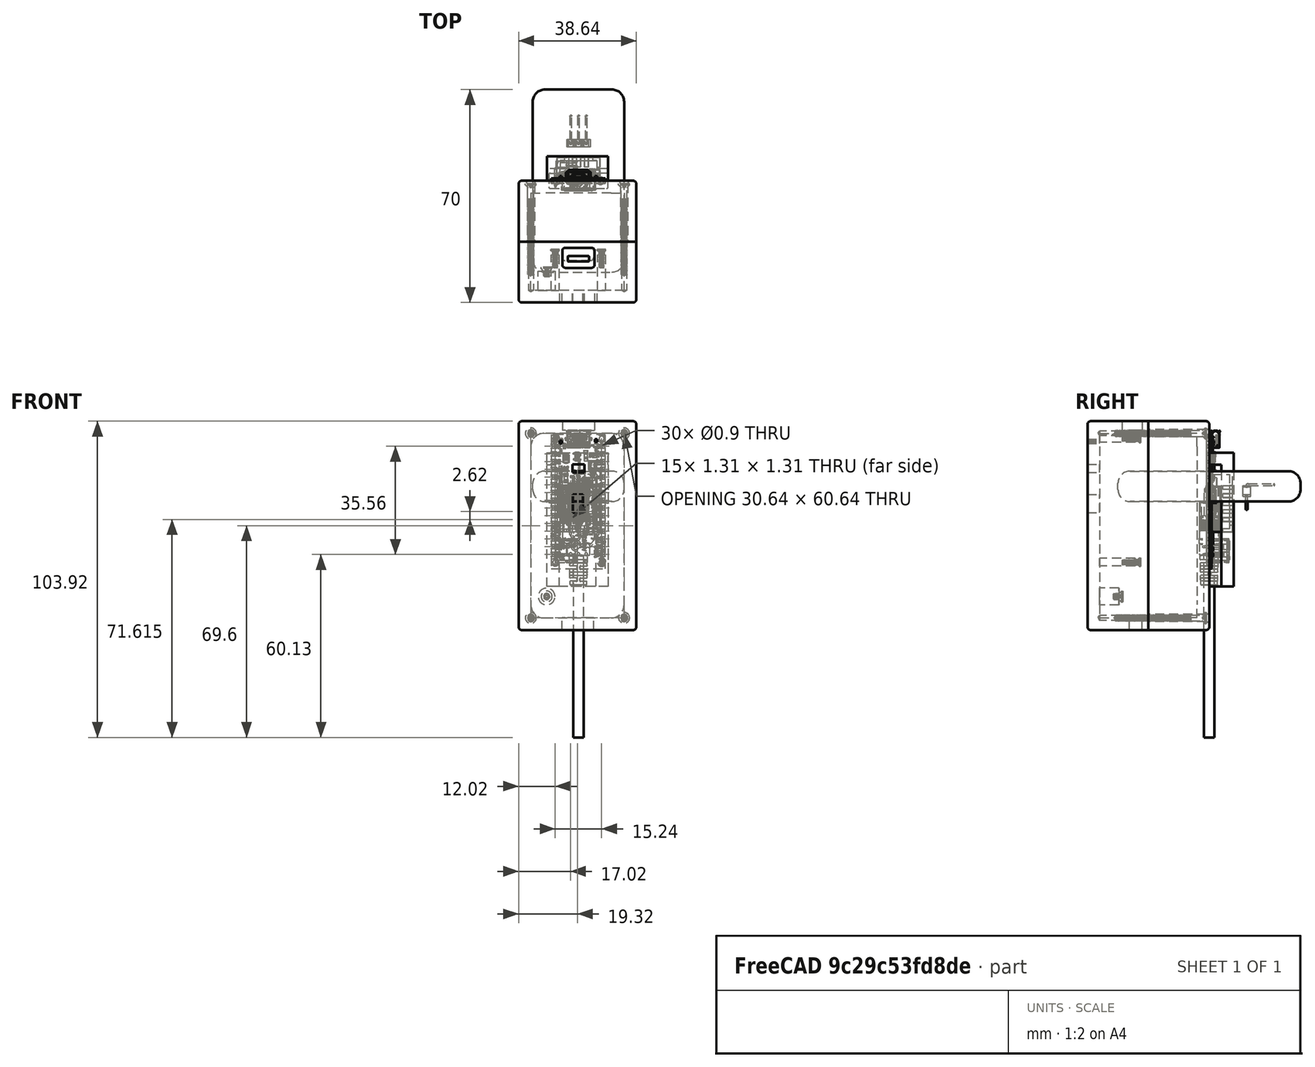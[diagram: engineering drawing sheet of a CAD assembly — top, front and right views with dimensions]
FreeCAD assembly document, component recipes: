
FREECAD ASSEMBLY — COMPONENT RECIPES ("iot_assembly")

This assembly document has 7 components, labeled P0..P6 below (a component is one placed body or linked part). 3 of them carry a construction recipe — the FreeCAD feature program that regenerates the part from scratch, quoted from this document or its linked companion documents; the rest are supplied as boundary geometry only. No exploded tour is included for this assembly.
COMPONENT P0 — geometry summary ("Part_ArduinoNano33IoT"; no construction recipe available for this part):
  bounding box: 45.3 x 17.8 x 5.6 mm
  tessellated surface: 86,666 triangles
  volume: 1530 mm^3 (34% of its bounding box)
COMPONENT P1 — geometry summary ("Part_DHT22Modulev3"; no construction recipe available for this part):
  bounding box: 25.6 x 14.0 x 7.7 mm
  tessellated surface: 5,666 triangles
  volume: 894 mm^3 (32% of its bounding box)
  symmetry: mirror-symmetric across its z mid-plane
COMPONENT P2 — geometry summary ("Part_MicroUSBCable"; no construction recipe available for this part):
  bounding box: 83.5 x 10.6 x 6.6 mm
  tessellated surface: 36,642 triangles
  volume: 1833 mm^3 (31% of its bounding box)
  symmetry: 2-fold rotationally symmetric about the z axis; mirror-symmetric across its x mid-plane, y mid-plane
COMPONENT P3 — recipe-attached ("Part_Battery", modeled in this document).
Construction recipe (the document's own serialized feature program — sketch geometry with constraints, then the solid features built on it; lengths are millimeters unless a unit is written):

FEATURE [Sketcher::SketchObject] Sketch
  ArcFitTolerance = 1e-06
  AttachmentSupport = -> [XY_Plane008]
  FullyConstrained = true
  MakeInternals = false
  MapMode = 5
  expr: Constraints[8] = <<Spreadsheet_Battery>>.BatteryWidth
  expr: Constraints[9] = <<Spreadsheet_Battery>>.BatteryLength
  sketch-geometry (4):
    g0: LineSegment StartX=-15 StartY=30 StartZ=0 EndX=-15 EndY=-30 EndZ=0
    g1: LineSegment StartX=-15 StartY=-30 StartZ=0 EndX=15 EndY=-30 EndZ=0
    g2: LineSegment StartX=15 StartY=-30 StartZ=0 EndX=15 EndY=30 EndZ=0
    g3: LineSegment StartX=15 StartY=30 StartZ=0 EndX=-15 EndY=30 EndZ=0
  constraints (11):
    c: Coincident(g0,g1)
    c: Coincident(g1,g2)
    c: Coincident(g2,g3)
    c: Coincident(g3,g0)
    c: Vertical(g0)
    c: Vertical(g2)
    c: Horizontal(g1)
    c: Horizontal(g3)
    c: DistanceX(g3,g3) = 30
    c: DistanceY(g0,g0) = 60
    c: Symmetric(g0,g1,g-1)
FEATURE [PartDesign::Pad] Pad
  Direction = (0,0,1)
  Length = 10
  Length2 = 10
  Profile = -> Sketch
  ReferenceAxis = -> Sketch [N_Axis]
  Refine = true
  Suppressed = false
  Type = 0
  expr: Length = <<Spreadsheet_Battery>>.BatteryHeight
FEATURE [PartDesign::Fillet] Fillet
  Base = -> Pad [Face6,Face5,Face4,Face1]
  BaseFeature = -> Pad
  Radius = 4
  Refine = true
  SupportTransform = false
  Suppressed = false
  UseAllEdges = true
FEATURE [PartDesign::Body] Body  label="Body_Battery"
  AllowCompound = false
  Group = -> [Sketch,Pad,Fillet]
  Origin = -> Origin008
  Tip = -> Fillet
COMPONENT P4 — recipe-attached ("Part_EnclosureBottom", modeled in this document).
Construction recipe (the document's own serialized feature program — sketch geometry with constraints, then the solid features built on it; lengths are millimeters unless a unit is written):

FEATURE [PartDesign::SubShapeBinder] Binder  label="Binder_Battery"
  BindCopyOnChange = 0
  BindMode = 0
  ClaimChildren = false
  Context = -> Assembly001 [Assembly002.Part001.Body001.Binder.]
  Fuse = false
  MakeFace = true
  OffsetFill = false
  OffsetIntersection = false
  OffsetJoinType = 0
  OffsetOpenResult = false
  PartialLoad = false
  Refine = true
  Relative = true
  Support = -> [Part]
  _Version = 2
FEATURE [Sketcher::SketchObject] Sketch001
  ArcFitTolerance = 1e-06
  AttachmentSupport = -> [XZ_Plane010]
  ExternalGeometry = -> [Binder]
  FullyConstrained = true
  MakeInternals = false
  MapMode = 5
  Placement = pos=(0,0,0) rot=(1,0,0;1.5708rad)
  expr: Constraints[10] = <<Spreadsheet_Enclosure>>.EnclosureWallThickness + <<Spreadsheet_Enclosure>>.EnclosureWallThicknessTolerance
  expr: Constraints[11] = <<Spreadsheet_Enclosure>>.EnclosureWallThickness + <<Spreadsheet_Enclosure>>.EnclosureWallThicknessTolerance
  expr: Constraints[8] = <<Spreadsheet_Enclosure>>.EnclosureWallThickness + <<Spreadsheet_Enclosure>>.EnclosureWallThicknessTolerance
  expr: Constraints[9] = <<Spreadsheet_Enclosure>>.EnclosureWallThickness + <<Spreadsheet_Enclosure>>.EnclosureWallThicknessTolerance
  sketch-geometry (4):
    g0: LineSegment StartX=-19.64 StartY=26.42 StartZ=0 EndX=-19.64 EndY=-42.22 EndZ=0
    g1: LineSegment StartX=-19.64 StartY=-42.22 StartZ=0 EndX=19 EndY=-42.22 EndZ=0
    g2: LineSegment StartX=19 StartY=-42.22 StartZ=0 EndX=19 EndY=26.42 EndZ=0
    g3: LineSegment StartX=19 StartY=26.42 StartZ=0 EndX=-19.64 EndY=26.42 EndZ=0
  constraints (12):
    c: Coincident(g0,g1)
    c: Coincident(g1,g2)
    c: Coincident(g2,g3)
    c: Coincident(g3,g0)
    c: Vertical(g0)
    c: Vertical(g2)
    c: Horizontal(g1)
    c: Horizontal(g3)
    c: Distance(g3,g-4) = 4.32
    c: Distance(g-10,g0) = 4.32
    c: Distance(g-6,g2) = 4.32
    c: Distance(g-8,g1) = 4.32
FEATURE [PartDesign::Pad] Pad001  label="EnclosureBottom"
  Direction = (0,-1,2e-16)
  Length = 20
  Length2 = 10
  Placement = pos=(0,0,0) rot=(1,0,0;1.5708rad)
  Profile = -> Sketch001
  ReferenceAxis = -> Sketch001 [N_Axis]
  Refine = true
  Suppressed = false
  Type = 0
  expr: Length = <<Spreadsheet_Enclosure>>.EnclosureBottomDepth
FEATURE [PartDesign::Thickness] Thickness  label="EnclosureWallThickness001"
  Base = -> Pad001 [Face6]
  BaseFeature = -> Pad001
  Intersection = false
  Join = 0
  Mode = 0
  Refine = true
  Reversed = true
  SupportTransform = false
  Suppressed = false
  Value = 4
  expr: Value = <<Spreadsheet_Enclosure>>.EnclosureWallThickness
FEATURE [PartDesign::Fillet] Fillet002  label="EnclosureFillet001"
  Base = -> Thickness [Edge1,Edge8,Edge5,Edge2,Edge3,Edge6,Edge9,Edge11]
  BaseFeature = -> Thickness
  Radius = 1
  Refine = true
  SupportTransform = false
  Suppressed = false
  UseAllEdges = false
  expr: Radius = <<Spreadsheet_Enclosure>>.EnclosureBevel
FEATURE [Sketcher::SketchObject] Sketch012
  ArcFitTolerance = 1e-06
  AttachmentSupport = -> [Fillet002]
  ExternalGeometry = -> [Binder,Fillet002]
  FullyConstrained = true
  MakeInternals = false
  MapMode = 5
  Placement = pos=(0,-4,0) rot=(1,0,0;1.5708rad)
  expr: Constraints[14] = <<Spreadsheet_Enclosure>>.EnclosureWallThickness + <<Spreadsheet_Enclosure>>.EnclosureWallThicknessTolerance
  expr: Constraints[1] = <<Spreadsheet_Enclosure>>.EnclosureWallThickness + <<Spreadsheet_Enclosure>>.EnclosureWallThicknessTolerance
  expr: Constraints[20] = <<Spreadsheet_Enclosure>>.EnclosureWallThickness + <<Spreadsheet_Enclosure>>.EnclosureWallThicknessTolerance
  expr: Constraints[8] = <<Spreadsheet_Enclosure>>.EnclosureWallThickness + <<Spreadsheet_Enclosure>>.EnclosureWallThicknessTolerance
  sketch-geometry (12):
    g0: ArcOfCircle CenterX=-11.32 CenterY=18.1 CenterZ=0 NormalX=0 NormalY=0 NormalZ=1 AngleXU=0 Radius=4.32 StartAngle=1.5708 EndAngle=3.14159
    g1: LineSegment StartX=-15.64 StartY=22.42 StartZ=0 EndX=-15.64 EndY=18.1 EndZ=0
    g2: LineSegment StartX=-11.32 StartY=22.42 StartZ=0 EndX=-15.64 EndY=22.42 EndZ=0
    g3: ArcOfCircle CenterX=10.68 CenterY=18.1 CenterZ=0 NormalX=0 NormalY=0 NormalZ=1 AngleXU=0 Radius=4.32 StartAngle=8.06468e-08 EndAngle=1.5708
    g4: LineSegment StartX=15 StartY=22.42 StartZ=0 EndX=15 EndY=18.1 EndZ=0
    g5: LineSegment StartX=10.68 StartY=22.42 StartZ=0 EndX=15 EndY=22.42 EndZ=0
    g6: ArcOfCircle CenterX=10.68 CenterY=-33.9 CenterZ=0 NormalX=0 NormalY=0 NormalZ=1 AngleXU=0 Radius=4.32 StartAngle=4.71239 EndAngle=6.28319
    g7: LineSegment StartX=10.68 StartY=-38.22 StartZ=0 EndX=15 EndY=-38.22 EndZ=0
    g8: LineSegment StartX=15 StartY=-38.22 StartZ=0 EndX=15 EndY=-33.9 EndZ=0
    g9: LineSegment StartX=-15.64 StartY=-38.22 StartZ=0 EndX=-15.64 EndY=-33.9 EndZ=0
    g10: ArcOfCircle CenterX=-11.32 CenterY=-33.9 CenterZ=0 NormalX=0 NormalY=0 NormalZ=1 AngleXU=0 Radius=4.32 StartAngle=3.14159 EndAngle=4.71239
    g11: LineSegment StartX=-11.32 StartY=-38.22 StartZ=0 EndX=-15.64 EndY=-38.22 EndZ=0
  constraints (32):
    c: Coincident(g0,g-3)
    c: Radius(g0) = 4.32
    c: Coincident(g2,g1)
    c: Vertical(g1)
    c: Horizontal(g2)
    c: Coincident(g1,g-5)
    c: Coincident(g0,g2)
    c: Coincident(g0,g1)
    c: Radius(g3) = 4.32
    c: Coincident(g5,g4)
    c: Vertical(g4)
    c: Horizontal(g5)
    c: Coincident(g3,g5)
    c: Coincident(g3,g4)
    c: Radius(g10) = 4.32
    c: Coincident(g11,g9)
    c: Vertical(g9)
    c: Horizontal(g11)
    c: Coincident(g10,g11)
    c: Coincident(g10,g9)
    c: Radius(g6) = 4.32
    c: Coincident(g7,g8)
    c: Vertical(g8)
    c: Horizontal(g7)
    c: Coincident(g6,g7)
    c: Coincident(g6,g8)
    c: Coincident(g-6,g3)
    c: Coincident(g4,g-9)
    c: Coincident(g7,g-10)
    c: Coincident(g6,g-8)
    c: Coincident(g9,g-10)
    c: Coincident(g10,g-7)
FEATURE [PartDesign::Pad] Pad006  label="EnclosureReinforcement"
  BaseFeature = -> Fillet002
  Direction = (0,-1,2e-16)
  Length = 10
  Length2 = 10
  Profile = -> Sketch012
  ReferenceAxis = -> Sketch012 [N_Axis]
  Refine = true
  Suppressed = false
  Type = 3
  UpToFace = -> Fillet002 [Face2]
FEATURE [Sketcher::SketchObject] Sketch013
  ArcFitTolerance = 1e-06
  AttachmentSupport = -> [Pad006]
  ExternalGeometry = -> [Pad006]
  FullyConstrained = true
  MakeInternals = false
  MapMode = 5
  Placement = pos=(0,-1.8e-15,0) rot=(0,0.707107,0.707107;3.14159rad)
  expr: Constraints[0] = <<Spreadsheet_Enclosure>>.EnclosureScrewHoles
  expr: Constraints[3] = <<Spreadsheet_Enclosure>>.EnclosureScrewHoles
  expr: Constraints[6] = <<Spreadsheet_Enclosure>>.EnclosureScrewHoles
  expr: Constraints[7] = <<Spreadsheet_Enclosure>>.EnclosureScrewHoles
  sketch-geometry (4):
    g0: Circle CenterX=-15 CenterY=22.42 CenterZ=0 NormalX=0 NormalY=0 NormalZ=1 AngleXU=0 Radius=1
    g1: Circle CenterX=15.64 CenterY=22.42 CenterZ=0 NormalX=0 NormalY=0 NormalZ=1 AngleXU=0 Radius=1
    g2: Circle CenterX=-15 CenterY=-38.22 CenterZ=0 NormalX=0 NormalY=0 NormalZ=1 AngleXU=0 Radius=1
    g3: Circle CenterX=15.64 CenterY=-38.22 CenterZ=0 NormalX=0 NormalY=0 NormalZ=1 AngleXU=0 Radius=1
  constraints (12):
    c: Diameter(g0) = 2
    c: Vertical(g0,g-8)
    c: Horizontal(g-9,g0)
    c: Diameter(g1) = 2
    c: Horizontal(g-10,g1)
    c: Vertical(g-11,g1)
    c: Diameter(g2) = 2
    c: Diameter(g3) = 2
    c: Vertical(g3,g-12)
    c: Horizontal(g3,g-13)
    c: Vertical(g-14,g2)
    c: Horizontal(g2,g-14)
FEATURE [PartDesign::Hole] Hole002  label="EnclosureScrewHoles"
  BaseFeature = -> Pad006
  CustomThreadClearance = 0
  Depth = 25
  DepthType = 0
  Diameter = 2.4
  DrillForDepth = false
  DrillPoint = 1
  DrillPointAngle = 118
  HoleCutCountersinkAngle = 90
  HoleCutCustomValues = false
  HoleCutDepth = 0
  HoleCutDiameter = 6.1
  HoleCutType = 0
  ModelThread = false
  Profile = -> Sketch013
  Refine = true
  Suppressed = false
  Tapered = false
  TaperedAngle = 90
  ThreadClass = 0
  ThreadDepth = 25
  ThreadDepthType = 0
  ThreadDirection = 0
  ThreadFit = 0
  ThreadSize = 6
  ThreadType = 1
  Threaded = false
  UseCustomThreadClearance = false
FEATURE [PartDesign::Fillet] Fillet004  label="EnclosureScrewHolesFillet"
  Base = -> Hole002 [Edge41,Edge45,Edge63,Edge43]
  BaseFeature = -> Hole002
  Radius = 1
  Refine = true
  SupportTransform = false
  Suppressed = false
  UseAllEdges = false
FEATURE [Sketcher::SketchObject] Sketch018
  ArcFitTolerance = 1e-06
  AttachmentSupport = -> [Fillet004]
  ExternalGeometry = -> [Fillet004]
  FullyConstrained = true
  MakeInternals = false
  MapMode = 5
  Placement = pos=(0,-1.8e-15,0) rot=(0,0.707107,0.707107;3.14159rad)
  expr: Constraints[8] = <<Spreadsheet_Enclosure>>.EnclosureSlidingMechanismWidth - <<Spreadsheet_Enclosure>>.EnclosureSlidingMechanismThickness * 2
  expr: Constraints[9] = <<Spreadsheet_Enclosure>>.EnclosureSlidingMechanismLength
  sketch-geometry (9):
    g0: LineSegment StartX=-5.68 StartY=12.1 StartZ=0 EndX=-5.68 EndY=-27.9 EndZ=0
    g1: LineSegment StartX=-5.68 StartY=-27.9 StartZ=0 EndX=6.32 EndY=-27.9 EndZ=0
    g2: LineSegment StartX=6.32 StartY=-27.9 StartZ=0 EndX=6.32 EndY=12.1 EndZ=0
    g3: LineSegment StartX=6.32 StartY=12.1 StartZ=0 EndX=-5.68 EndY=12.1 EndZ=0
    g4: LineSegment [constr] StartX=-18 StartY=25.42 StartZ=0 EndX=-18 EndY=-41.22 EndZ=0
    g5: LineSegment [constr] StartX=-18 StartY=-41.22 StartZ=0 EndX=18.64 EndY=-41.22 EndZ=0
    g6: LineSegment [constr] StartX=18.64 StartY=-41.22 StartZ=0 EndX=18.64 EndY=25.42 EndZ=0
    g7: LineSegment [constr] StartX=18.64 StartY=25.42 StartZ=0 EndX=-18 EndY=25.42 EndZ=0
    g8: GeomPoint [constr] X=0.32 Y=-7.9 Z=0
  constraints (22):
    c: Coincident(g0,g1)
    c: Coincident(g1,g2)
    c: Coincident(g2,g3)
    c: Coincident(g3,g0)
    c: Vertical(g0)
    c: Vertical(g2)
    c: Horizontal(g1)
    c: Horizontal(g3)
    c: DistanceX(g3,g3) = 12
    c: DistanceY(g0,g0) = 40
    c: Coincident(g4,g5)
    c: Coincident(g5,g6)
    c: Coincident(g6,g7)
    c: Coincident(g7,g4)
    c: Vertical(g4)
    c: Vertical(g6)
    c: Horizontal(g5)
    c: Horizontal(g7)
    c: Coincident(g4,g-3)
    c: Coincident(g5,g-4)
    c: Symmetric(g5,g4,g8)
    c: Symmetric(g0,g1,g8)
FEATURE [PartDesign::Pad] Pad008  label="EnclosureSlidingMechanismSupport"
  BaseFeature = -> Fillet004
  Direction = (0,1,-2e-16)
  Length = 4
  Length2 = 10
  Profile = -> Sketch018
  ReferenceAxis = -> Sketch018 [N_Axis]
  Refine = true
  Suppressed = false
  Type = 0
  expr: Length = <<Spreadsheet_Enclosure>>.EnclosureSlidingMechanismThickness
FEATURE [Sketcher::SketchObject] Sketch019
  ArcFitTolerance = 1e-06
  AttachmentSupport = -> [Pad008]
  ExternalGeometry = -> [Pad008]
  FullyConstrained = true
  MakeInternals = false
  MapMode = 5
  Placement = pos=(0,4,0) rot=(0,0.707107,0.707107;3.14159rad)
  expr: Constraints[8] = <<Spreadsheet_Enclosure>>.EnclosureSlidingMechanismWidth
  expr: Constraints[9] = <<Spreadsheet_Enclosure>>.EnclosureSlidingMechanismLength
  sketch-geometry (9):
    g0: LineSegment StartX=-9.68 StartY=12.1 StartZ=0 EndX=-9.68 EndY=-27.9 EndZ=0
    g1: LineSegment StartX=-9.68 StartY=-27.9 StartZ=0 EndX=10.32 EndY=-27.9 EndZ=0
    g2: LineSegment StartX=10.32 StartY=-27.9 StartZ=0 EndX=10.32 EndY=12.1 EndZ=0
    g3: LineSegment StartX=10.32 StartY=12.1 StartZ=0 EndX=-9.68 EndY=12.1 EndZ=0
    g4: LineSegment [constr] StartX=-18 StartY=25.42 StartZ=0 EndX=-18 EndY=-41.22 EndZ=0
    g5: LineSegment [constr] StartX=-18 StartY=-41.22 StartZ=0 EndX=18.64 EndY=-41.22 EndZ=0
    g6: LineSegment [constr] StartX=18.64 StartY=-41.22 StartZ=0 EndX=18.64 EndY=25.42 EndZ=0
    g7: LineSegment [constr] StartX=18.64 StartY=25.42 StartZ=0 EndX=-18 EndY=25.42 EndZ=0
    g8: GeomPoint [constr] X=0.32 Y=-7.9 Z=0
  constraints (22):
    c: Coincident(g0,g1)
    c: Coincident(g1,g2)
    c: Coincident(g2,g3)
    c: Coincident(g3,g0)
    c: Vertical(g0)
    c: Vertical(g2)
    c: Horizontal(g1)
    c: Horizontal(g3)
    c: DistanceX(g3,g3) = 20
    c: DistanceY(g0,g0) = 40
    c: Coincident(g4,g5)
    c: Coincident(g5,g6)
    c: Coincident(g6,g7)
    c: Coincident(g7,g4)
    c: Vertical(g4)
    c: Vertical(g6)
    c: Horizontal(g5)
    c: Horizontal(g7)
    c: Coincident(g4,g-3)
    c: Coincident(g5,g-4)
    c: Symmetric(g4,g5,g8)
    c: Symmetric(g1,g0,g8)
FEATURE [PartDesign::Pad] Pad009  label="EnclosureSlidingMechanismSupportMaleChannel"
  BaseFeature = -> Pad008
  Direction = (0,1,-2e-16)
  Length = 4
  Length2 = 10
  Profile = -> Sketch019
  ReferenceAxis = -> Sketch019 [N_Axis]
  Refine = true
  Suppressed = false
  Type = 0
  expr: Length = <<Spreadsheet_Enclosure>>.EnclosureSlidingMechanismChannel
FEATURE [Sketcher::SketchObject] Sketch020
  ArcFitTolerance = 1e-06
  AttachmentSupport = -> [Pad009]
  ExternalGeometry = -> [Pad009]
  FullyConstrained = true
  MakeInternals = false
  MapMode = 5
  Placement = pos=(0,0,12.1) rot=(0,0,1;0rad)
  sketch-geometry (4):
    g0: LineSegment StartX=-10.32 StartY=8 StartZ=0 EndX=-10.32 EndY=0 EndZ=0
    g1: LineSegment StartX=-10.32 StartY=0 StartZ=0 EndX=9.68 EndY=0 EndZ=0
    g2: LineSegment StartX=9.68 StartY=0 StartZ=0 EndX=9.68 EndY=8 EndZ=0
    g3: LineSegment StartX=9.68 StartY=8 StartZ=0 EndX=-10.32 EndY=8 EndZ=0
  constraints (11):
    c: Coincident(g0,g1)
    c: Coincident(g1,g2)
    c: Coincident(g2,g3)
    c: Coincident(g3,g0)
    c: Vertical(g0)
    c: Vertical(g2)
    c: Horizontal(g1)
    c: Horizontal(g3)
    c: Coincident(g0,g-3)
    c: Vertical(g1,g-4)
    c: Horizontal(g1,g-1)
FEATURE [PartDesign::Pad] Pad010  label="EnclosureSlidingMechanismStop"
  BaseFeature = -> Pad009
  Direction = (0,0,1)
  Length = 4
  Length2 = 10
  Profile = -> Sketch020
  ReferenceAxis = -> Sketch020 [N_Axis]
  Refine = true
  Suppressed = false
  Type = 0
  expr: Length = <<Spreadsheet_Enclosure>>.EnclosureSlidingMechanismThickness
FEATURE [PartDesign::Body] Body001  label="Body_EnclosureBottom"
  AllowCompound = false
  Group = -> [Binder,Sketch001,Pad001,Thickness,Fillet002,Sketch012,Pad006,Sketch013,Hole002,Fillet004,Sketch018,Pad008,Sketch019,Pad009,Sketch020,Pad010]
  Origin = -> Origin010
  Tip = -> Pad010
COMPONENT P5 — recipe-attached ("Part_EnclosureTop", modeled in this document).
Construction recipe (the document's own serialized feature program — sketch geometry with constraints, then the solid features built on it; lengths are millimeters unless a unit is written):

FEATURE [PartDesign::SubShapeBinder] Binder001  label="Binder_EnclosureBottom"
  BindCopyOnChange = 0
  BindMode = 0
  ClaimChildren = false
  Context = -> Assembly001 [Assembly002.Part002.Body002.Binder001.]
  Fuse = false
  MakeFace = true
  OffsetFill = false
  OffsetIntersection = false
  OffsetJoinType = 0
  OffsetOpenResult = false
  PartialLoad = false
  Refine = true
  Relative = true
  Support = -> [Part001]
  _Version = 2
FEATURE [Sketcher::SketchObject] Sketch002
  ArcFitTolerance = 1e-06
  AttachmentSupport = -> [Binder001]
  ExternalGeometry = -> [Binder001]
  FullyConstrained = true
  MakeInternals = false
  MapMode = 5
  Placement = pos=(0,-20,5.2e-15) rot=(1,0,0;1.5708rad)
  sketch-geometry (4):
    g0: LineSegment StartX=-19.64 StartY=26.42 StartZ=0 EndX=-19.64 EndY=-42.22 EndZ=0
    g1: LineSegment StartX=-19.64 StartY=-42.22 StartZ=0 EndX=19 EndY=-42.22 EndZ=0
    g2: LineSegment StartX=19 StartY=-42.22 StartZ=0 EndX=19 EndY=26.42 EndZ=0
    g3: LineSegment StartX=19 StartY=26.42 StartZ=0 EndX=-19.64 EndY=26.42 EndZ=0
  constraints (12):
    c: Coincident(g0,g1)
    c: Coincident(g1,g2)
    c: Coincident(g2,g3)
    c: Coincident(g3,g0)
    c: Vertical(g0)
    c: Vertical(g2)
    c: Horizontal(g1)
    c: Horizontal(g3)
    c: Horizontal(g0,g-4)
    c: Horizontal(g0,g-6)
    c: Vertical(g-5,g0)
    c: Vertical(g-7,g2)
FEATURE [PartDesign::Pad] Pad002  label="EnclosureTop"
  Direction = (0,-1,2e-16)
  Length = 20
  Length2 = 10
  Profile = -> Sketch002
  ReferenceAxis = -> Sketch002 [N_Axis]
  Refine = true
  Suppressed = false
  Type = 0
  expr: Length = <<Spreadsheet_Enclosure>>.EnclosureTopDepth
FEATURE [PartDesign::Thickness] Thickness001  label="EnclosureWallThickness"
  Base = -> Pad002 [Face5]
  BaseFeature = -> Pad002
  Intersection = false
  Join = 0
  Mode = 0
  Refine = true
  Reversed = true
  SupportTransform = false
  Suppressed = false
  Value = 4
  expr: Value = <<Spreadsheet_Enclosure>>.EnclosureWallThickness
FEATURE [PartDesign::SubShapeBinder] Binder002  label="Binder_ArduinoNano"
  BindCopyOnChange = 0
  BindMode = 0
  ClaimChildren = false
  Context = -> Assembly001 [Assembly002.Part002.Body002.Binder002.]
  Fuse = false
  MakeFace = true
  OffsetFill = false
  OffsetIntersection = false
  OffsetJoinType = 0
  OffsetOpenResult = false
  PartialLoad = false
  Refine = true
  Relative = true
  Support = -> [Assembly]
  _Version = 2
FEATURE [PartDesign::SubShapeBinder] Binder003  label="Binder_DHT22"
  BindCopyOnChange = 0
  BindMode = 0
  ClaimChildren = false
  Context = -> Assembly001 [Assembly002.Part002.Body002.Binder003.]
  Fuse = false
  MakeFace = true
  OffsetFill = false
  OffsetIntersection = false
  OffsetJoinType = 0
  OffsetOpenResult = false
  PartialLoad = false
  Refine = true
  Relative = true
  Support = -> [DHT22_Module_v3]
  _Version = 2
FEATURE [Sketcher::SketchObject] Sketch003
  ArcFitTolerance = 1e-06
  AttachmentSupport = -> [Thickness001,Binder002]
  ExternalGeometry = -> [Binder002]
  FullyConstrained = true
  MakeInternals = false
  MapMode = 5
  Placement = pos=(0,-36,9.4e-15) rot=(0,0.707107,0.707107;3.14159rad)
  sketch-geometry (4):
    g0: Circle CenterX=-7.62 CenterY=20.73 CenterZ=0 NormalX=0 NormalY=0 NormalZ=1 AngleXU=0 Radius=1.27
    g1: Circle CenterX=7.62 CenterY=20.73 CenterZ=0 NormalX=0 NormalY=0 NormalZ=1 AngleXU=0 Radius=1.27
    g2: Circle CenterX=-7.62 CenterY=-19.91 CenterZ=0 NormalX=0 NormalY=0 NormalZ=1 AngleXU=0 Radius=1.27
    g3: Circle CenterX=7.62 CenterY=-19.91 CenterZ=0 NormalX=0 NormalY=0 NormalZ=1 AngleXU=0 Radius=1.27
  constraints (8):
    c: Coincident(g0,g-3)
    c: Tangent(g0,g-7)
    c: Coincident(g1,g-13)
    c: Tangent(g1,g-5)
    c: Coincident(g2,g-12)
    c: Tangent(g2,g-11)
    c: Coincident(g3,g-8)
    c: Tangent(g3,g-9)
FEATURE [PartDesign::Pad] Pad003  label="PCBStandoffs"
  BaseFeature = -> Thickness001
  Direction = (0,1,-2e-16)
  Length = 10
  Length2 = 10
  Profile = -> Sketch003
  ReferenceAxis = -> Sketch003 [N_Axis]
  Refine = true
  Suppressed = false
  Type = 3
  UpToFace = -> Binder002 [Face2229]
FEATURE [Sketcher::SketchObject] Sketch004
  ArcFitTolerance = 1e-06
  AttachmentSupport = -> [Pad003]
  ExternalGeometry = -> [Binder002]
  FullyConstrained = true
  MakeInternals = false
  MapMode = 5
  Placement = pos=(0,-36,9.4e-15) rot=(0,0.707107,0.707107;3.14159rad)
  sketch-geometry (2):
    g0: Circle CenterX=-7.62 CenterY=20.73 CenterZ=0 NormalX=0 NormalY=0 NormalZ=1 AngleXU=0 Radius=0.8
    g1: Circle CenterX=7.62 CenterY=-19.91 CenterZ=0 NormalX=0 NormalY=0 NormalZ=1 AngleXU=0 Radius=0.8
  constraints (4):
    c: Coincident(g0,g-3)
    c: PointOnObject(g-3,g0)
    c: Coincident(g1,g-4)
    c: PointOnObject(g-4,g1)
FEATURE [PartDesign::Pad] Pad004  label="PCBPins"
  BaseFeature = -> Pad003
  Direction = (0,1,-2e-16)
  Length = 10
  Length2 = 10
  Profile = -> Sketch004
  ReferenceAxis = -> Sketch004 [N_Axis]
  Refine = true
  Suppressed = false
  Type = 3
  UpToFace = -> Binder002 [Face1966]
FEATURE [Sketcher::SketchObject] Sketch005
  ArcFitTolerance = 1e-06
  AttachmentSupport = -> [Pad004]
  ExternalGeometry = -> [Binder002]
  FullyConstrained = true
  MakeInternals = false
  MapMode = 5
  Placement = pos=(0,-24.35,0) rot=(0,0.707107,0.707107;3.14159rad)
  sketch-geometry (2):
    g0: Circle CenterX=-7.62 CenterY=-19.91 CenterZ=0 NormalX=0 NormalY=0 NormalZ=1 AngleXU=0 Radius=0.8
    g1: Circle CenterX=7.62 CenterY=20.73 CenterZ=0 NormalX=0 NormalY=0 NormalZ=1 AngleXU=0 Radius=0.8
  constraints (4):
    c: Coincident(g0,g-4)
    c: Equal(g0,g-4)
    c: Coincident(g1,g-3)
    c: Equal(g1,g-3)
FEATURE [PartDesign::Hole] Hole  label="PCBScrewHoles"
  BaseFeature = -> Pad004
  CustomThreadClearance = 0
  Depth = 2
  DepthType = 0
  Diameter = 0.75
  DrillForDepth = false
  DrillPoint = 1
  DrillPointAngle = 118
  HoleCutCountersinkAngle = 90
  HoleCutCustomValues = false
  HoleCutDepth = 0
  HoleCutDiameter = 6.1
  HoleCutType = 0
  ModelThread = false
  Profile = -> Sketch005
  Refine = true
  Suppressed = false
  Tapered = false
  TaperedAngle = 90
  ThreadClass = 0
  ThreadDepth = 2
  ThreadDepthType = 0
  ThreadDirection = 0
  ThreadFit = 0
  ThreadSize = 0
  ThreadType = 1
  Threaded = true
  UseCustomThreadClearance = false
FEATURE [Sketcher::SketchObject] Sketch006
  ArcFitTolerance = 1e-06
  AttachmentSupport = -> [Hole]
  ExternalGeometry = -> [Binder003]
  FullyConstrained = true
  MakeInternals = false
  MapMode = 5
  Placement = pos=(0,-36,9.4e-15) rot=(0,0.707107,0.707107;3.14159rad)
  sketch-geometry (1):
    g0: Circle CenterX=10.46 CenterY=-31.1889 CenterZ=0 NormalX=0 NormalY=0 NormalZ=1 AngleXU=0 Radius=2.75
  constraints (2):
    c: Coincident(g0,g-3)
    c: Tangent(g0,g-4)
FEATURE [PartDesign::Pad] Pad005  label="DHT22Standoff"
  BaseFeature = -> Hole
  Direction = (0,1,-2e-16)
  Length = 10
  Length2 = 10
  Profile = -> Sketch006
  ReferenceAxis = -> Sketch006 [N_Axis]
  Refine = true
  Suppressed = false
  Type = 3
  UpToFace = -> Binder003 [Face161]
FEATURE [Sketcher::SketchObject] Sketch007
  ArcFitTolerance = 1e-06
  AttachmentSupport = -> [Pad005]
  ExternalGeometry = -> [Binder003]
  FullyConstrained = true
  MakeInternals = false
  MapMode = 5
  Placement = pos=(0,-29.7,1.57e-14) rot=(0,0.707107,0.707107;3.14159rad)
  sketch-geometry (1):
    g0: Circle CenterX=10.46 CenterY=-31.1889 CenterZ=0 NormalX=0 NormalY=0 NormalZ=1 AngleXU=0 Radius=1.55
  constraints (2):
    c: Coincident(g0,g-3)
    c: PointOnObject(g-3,g0)
FEATURE [PartDesign::Hole] Hole001  label="DHT22ScrewHole"
  BaseFeature = -> Pad005
  CustomThreadClearance = 0
  Depth = 1
  DepthType = 0
  Diameter = 1.6
  DrillForDepth = false
  DrillPoint = 1
  DrillPointAngle = 118
  HoleCutCountersinkAngle = 90
  HoleCutCustomValues = false
  HoleCutDepth = 0
  HoleCutDiameter = 6.1
  HoleCutType = 0
  ModelThread = false
  Profile = -> Sketch007
  Refine = true
  Suppressed = false
  Tapered = false
  TaperedAngle = 90
  ThreadClass = 0
  ThreadDepth = 1
  ThreadDepthType = 0
  ThreadDirection = 0
  ThreadFit = 0
  ThreadSize = 6
  ThreadType = 1
  Threaded = true
  UseCustomThreadClearance = false
FEATURE [Sketcher::SketchObject] Sketch008
  ArcFitTolerance = 1e-06
  AttachmentSupport = -> [Hole001]
  ExternalGeometry = -> [Hole001,Binder003]
  FullyConstrained = true
  MakeInternals = false
  MapMode = 5
  Placement = pos=(0,-9.3e-15,-42.22) rot=(1,0,0;3.14159rad)
  sketch-geometry (4):
    g0: LineSegment StartX=-5.38001 StartY=26.2 StartZ=0 EndX=-5.38001 EndY=22 EndZ=0
    g1: LineSegment StartX=-5.38001 StartY=22 StartZ=0 EndX=5 EndY=22 EndZ=0
    g2: LineSegment StartX=5 StartY=22 StartZ=0 EndX=5 EndY=26.2 EndZ=0
    g3: LineSegment StartX=5 StartY=26.2 StartZ=0 EndX=-5.38001 EndY=26.2 EndZ=0
  constraints (12):
    c: Coincident(g0,g1)
    c: Coincident(g1,g2)
    c: Coincident(g2,g3)
    c: Coincident(g3,g0)
    c: Vertical(g0)
    c: Vertical(g2)
    c: Horizontal(g1)
    c: Horizontal(g3)
    c: Distance(g1,g-3) = 2
    c: Distance(g3,g-4) = 1
    c: Distance(g2,g-2) = 5
    c: Equal(g2,g0)
FEATURE [PartDesign::Pocket] Pocket  label="DHT22Opening"
  BaseFeature = -> Hole001
  Direction = (0,0,1)
  Length = 0
  Length2 = 5
  Profile = -> Sketch008
  ReferenceAxis = -> Sketch008 [N_Axis]
  Refine = true
  Suppressed = false
  Type = 2
FEATURE [Sketcher::SketchObject] Sketch009
  ArcFitTolerance = 1e-06
  AttachmentSupport = -> [Pocket]
  ExternalGeometry = -> [Binder002]
  FullyConstrained = true
  MakeInternals = false
  MapMode = 5
  Placement = pos=(0,5.8e-15,26.42) rot=(0,0,1;0rad)
  sketch-geometry (8):
    g0: LineSegment StartX=-3.25 StartY=-24.7 StartZ=0 EndX=3.25 EndY=-24.7 EndZ=0
    g1: LineSegment StartX=3.45 StartY=-24.9 StartZ=0 EndX=3.45 EndY=-26.35 EndZ=0
    g2: LineSegment StartX=-3.25 StartY=-26.55 StartZ=0 EndX=3.25 EndY=-26.55 EndZ=0
    g3: LineSegment StartX=-3.45 StartY=-26.35 StartZ=0 EndX=-3.45 EndY=-24.9 EndZ=0
    g4: ArcOfCircle CenterX=-3.25 CenterY=-24.9 CenterZ=0 NormalX=0 NormalY=0 NormalZ=1 AngleXU=0 Radius=0.2 StartAngle=1.5708 EndAngle=3.14159
    g5: ArcOfCircle CenterX=-3.25 CenterY=-26.35 CenterZ=0 NormalX=0 NormalY=0 NormalZ=1 AngleXU=0 Radius=0.2 StartAngle=3.14159 EndAngle=4.71239
    g6: ArcOfCircle CenterX=3.25 CenterY=-24.9 CenterZ=0 NormalX=0 NormalY=0 NormalZ=1 AngleXU=0 Radius=0.2 StartAngle=7.6e-15 EndAngle=1.5708
    g7: ArcOfCircle CenterX=3.25 CenterY=-26.35 CenterZ=0 NormalX=0 NormalY=0 NormalZ=1 AngleXU=0 Radius=0.2 StartAngle=4.71239 EndAngle=6.28319
  constraints (16):
    c: Coincident(g7,g-3)
    c: Tangent(g-3,g7) = -1.5708
    c: Tangent(g6,g-4) = -1.5708
    c: Coincident(g6,g-4)
    c: Coincident(g0,g6)
    c: Coincident(g7,g2)
    c: Coincident(g1,g6)
    c: Coincident(g7,g1)
    c: Coincident(g-6,g4)
    c: Tangent(g-6,g4) = -1.5708
    c: Coincident(g5,g-5)
    c: Tangent(g-5,g5) = -1.5708
    c: Coincident(g4,g0)
    c: Coincident(g5,g2)
    c: Coincident(g3,g4)
    c: Coincident(g5,g3)
FEATURE [PartDesign::Pocket] Pocket001  label="MicroUSBConnectorOpening"
  BaseFeature = -> Pocket
  Direction = (0,0,-1)
  Length = 4
  Length2 = 5
  Profile = -> Sketch009
  ReferenceAxis = -> Sketch009 [N_Axis]
  Refine = true
  Suppressed = false
  Type = 0
FEATURE [PartDesign::SubShapeBinder] Binder004  label="Binder_MicroUSBCable"
  BindCopyOnChange = 0
  BindMode = 0
  ClaimChildren = false
  Context = -> Assembly001 [Assembly002.Part002.Body002.Binder004.]
  Fuse = false
  MakeFace = true
  OffsetFill = false
  OffsetIntersection = false
  OffsetJoinType = 0
  OffsetOpenResult = false
  PartialLoad = false
  Refine = true
  Relative = true
  Support = -> [Micro_USB_Plug_v10]
  _Version = 2
FEATURE [Sketcher::SketchObject] Sketch010
  ArcFitTolerance = 1e-06
  AttachmentSupport = -> [Pocket001]
  ExternalGeometry = -> [Pocket001]
  FullyConstrained = true
  MakeInternals = false
  MapMode = 5
  Placement = pos=(0,5.8e-15,26.42) rot=(0,0,1;0rad)
  sketch-geometry (4):
    g0: LineSegment StartX=5.3 StartY=-28.6 StartZ=0 EndX=-5.3 EndY=-28.6 EndZ=0
    g1: LineSegment StartX=5.3 StartY=-22 StartZ=0 EndX=5.3 EndY=-28.6 EndZ=0
    g2: LineSegment StartX=5.3 StartY=-22 StartZ=0 EndX=-5.3 EndY=-22 EndZ=0
    g3: LineSegment StartX=-5.3 StartY=-28.6 StartZ=0 EndX=-5.3 EndY=-22 EndZ=0
  constraints (12):
    c: Distance(g2,g0) = 6.6
    c: Distance(g1,g3) = 10.6
    c: Distance(g-3,g2) = 2
    c: Horizontal(g2)
    c: Horizontal(g0)
    c: Vertical(g1)
    c: Vertical(g3)
    c: Coincident(g1,g2)
    c: Coincident(g0,g1)
    c: Coincident(g3,g0)
    c: Coincident(g2,g3)
    c: Distance(g1,g-2) = 5.3
FEATURE [PartDesign::Pocket] Pocket002  label="MicroUSBConnectorBodyOpening"
  BaseFeature = -> Pocket001
  Direction = (0,0,-1)
  Length = 3
  Length2 = 5
  Profile = -> Sketch010
  ReferenceAxis = -> Sketch010 [N_Axis]
  Refine = true
  Suppressed = false
  Type = 0
FEATURE [PartDesign::Fillet] Fillet001  label="OpeningFillets"
  Base = -> Pocket002 [Edge33,Edge39,Edge35,Edge37,Edge25,Edge30,Edge28,Edge26]
  BaseFeature = -> Pocket002
  Radius = 1
  Refine = true
  SupportTransform = false
  Suppressed = false
  UseAllEdges = false
FEATURE [Sketcher::SketchObject] Sketch011
  ArcFitTolerance = 1e-06
  AttachmentSupport = -> [Fillet001]
  ExternalGeometry = -> [Binder002]
  FullyConstrained = true
  MakeInternals = false
  MapMode = 5
  Placement = pos=(0,-40,1.04e-14) rot=(1,0,0;1.5708rad)
  sketch-geometry (8):
    g0: LineSegment StartX=-6.14626 StartY=20.0563 StartZ=0 EndX=-6.14626 EndY=19.1437 EndZ=0
    g1: LineSegment StartX=-6.14626 StartY=19.1437 StartZ=0 EndX=-5.43374 EndY=19.1437 EndZ=0
    g2: LineSegment StartX=-5.43374 StartY=19.1437 StartZ=0 EndX=-5.43374 EndY=20.0563 EndZ=0
    g3: LineSegment StartX=-5.43374 StartY=20.0563 StartZ=0 EndX=-6.14626 EndY=20.0563 EndZ=0
    g4: LineSegment StartX=5.45374 StartY=20.5563 StartZ=0 EndX=5.45374 EndY=19.6437 EndZ=0
    g5: LineSegment StartX=5.45374 StartY=19.6437 StartZ=0 EndX=6.16626 EndY=19.6437 EndZ=0
    g6: LineSegment StartX=6.16626 StartY=19.6437 StartZ=0 EndX=6.16626 EndY=20.5563 EndZ=0
    g7: LineSegment StartX=6.16626 StartY=20.5563 StartZ=0 EndX=5.45374 EndY=20.5563 EndZ=0
  constraints (20):
    c: Coincident(g0,g1)
    c: Coincident(g1,g2)
    c: Coincident(g2,g3)
    c: Coincident(g3,g0)
    c: Vertical(g0)
    c: Vertical(g2)
    c: Horizontal(g1)
    c: Horizontal(g3)
    c: Coincident(g0,g-3)
    c: Coincident(g1,g-4)
    c: Coincident(g4,g5)
    c: Coincident(g5,g6)
    c: Coincident(g6,g7)
    c: Coincident(g7,g4)
    c: Vertical(g4)
    c: Vertical(g6)
    c: Horizontal(g5)
    c: Horizontal(g7)
    c: Coincident(g4,g-7)
    c: Coincident(g5,g-8)
FEATURE [PartDesign::Pocket] Pocket003  label="LEDHoles"
  BaseFeature = -> Fillet001
  Direction = (0,1,-2e-16)
  Length = 5
  Length2 = 5
  Profile = -> Sketch011
  ReferenceAxis = -> Sketch011 [N_Axis]
  Refine = true
  Suppressed = false
  Type = 1
FEATURE [PartDesign::Fillet] Fillet003  label="EnclosureFillet"
  Base = -> Pocket003 [Edge12,Edge48,Edge29,Edge39,Edge31,Edge9,Edge38,Edge11]
  BaseFeature = -> Pocket003
  Radius = 1
  Refine = true
  SupportTransform = false
  Suppressed = false
  UseAllEdges = false
  expr: Radius = <<Spreadsheet_Enclosure>>.EnclosureBevel
FEATURE [Sketcher::SketchObject] Sketch014
  ArcFitTolerance = 1e-06
  AttachmentSupport = -> [Fillet003]
  ExternalGeometry = -> [Binder001,Fillet003]
  FullyConstrained = true
  MakeInternals = false
  MapMode = 5
  Placement = pos=(0,-36,9.4e-15) rot=(0,0.707107,0.707107;3.14159rad)
  expr: Constraints[11] = <<Spreadsheet_Enclosure>>.EnclosureWallThickness + <<Spreadsheet_Enclosure>>.EnclosureWallThicknessTolerance
  expr: Constraints[19] = <<Spreadsheet_Enclosure>>.EnclosureWallThickness + <<Spreadsheet_Enclosure>>.EnclosureWallThicknessTolerance
  expr: Constraints[23] = <<Spreadsheet_Enclosure>>.EnclosureWallThickness + <<Spreadsheet_Enclosure>>.EnclosureWallThicknessTolerance
  expr: Constraints[5] = <<Spreadsheet_Enclosure>>.EnclosureWallThickness + <<Spreadsheet_Enclosure>>.EnclosureWallThicknessTolerance
  sketch-geometry (12):
    g0: ArcOfCircle CenterX=-10.68 CenterY=18.1 CenterZ=0 NormalX=0 NormalY=0 NormalZ=1 AngleXU=0 Radius=4.32 StartAngle=1.5708 EndAngle=3.14159
    g1: LineSegment StartX=-15 StartY=18.1 StartZ=0 EndX=-15 EndY=22.42 EndZ=0
    g2: LineSegment StartX=-15 StartY=22.42 StartZ=0 EndX=-10.68 EndY=22.42 EndZ=0
    g3: ArcOfCircle CenterX=11.32 CenterY=18.1 CenterZ=0 NormalX=0 NormalY=0 NormalZ=1 AngleXU=0 Radius=4.32 StartAngle=3.58653e-06 EndAngle=1.5708
    g4: LineSegment StartX=15.64 StartY=18.1 StartZ=0 EndX=15.64 EndY=22.42 EndZ=0
    g5: LineSegment StartX=15.64 StartY=22.42 StartZ=0 EndX=11.32 EndY=22.42 EndZ=0
    g6: ArcOfCircle CenterX=-10.68 CenterY=-33.9 CenterZ=0 NormalX=0 NormalY=0 NormalZ=1 AngleXU=0 Radius=4.32 StartAngle=3.14159 EndAngle=4.71238
    g7: LineSegment StartX=-15 StartY=-38.22 StartZ=0 EndX=-10.68 EndY=-38.22 EndZ=0
    g8: LineSegment StartX=-15 StartY=-33.9 StartZ=0 EndX=-15 EndY=-38.22 EndZ=0
    g9: ArcOfCircle CenterX=11.32 CenterY=-33.9 CenterZ=0 NormalX=0 NormalY=0 NormalZ=1 AngleXU=0 Radius=4.32 StartAngle=4.71239 EndAngle=6.28319
    g10: LineSegment StartX=15.64 StartY=-38.22 StartZ=0 EndX=11.32 EndY=-38.22 EndZ=0
    g11: LineSegment StartX=15.64 StartY=-33.9 StartZ=0 EndX=15.64 EndY=-38.22 EndZ=0
  constraints (32):
    c: Coincident(g1,g2)
    c: Coincident(g-11,g1)
    c: Coincident(g0,g2)
    c: Coincident(g1,g0)
    c: Coincident(g-8,g0)
    c: Radius(g0) = 4.32
    c: Horizontal(g0,g-8)
    c: Vertical(g0,g-8)
    c: Coincident(g4,g5)
    c: Coincident(g3,g5)
    c: Coincident(g4,g3)
    c: Radius(g3) = 4.32
    c: Coincident(g3,g-12)
    c: Coincident(g4,g-14)
    c: Horizontal(g3,g-12)
    c: Vertical(g3,g-12)
    c: Coincident(g8,g7)
    c: Coincident(g6,g7)
    c: Coincident(g8,g6)
    c: Radius(g6) = 4.32
    c: Coincident(g11,g10)
    c: Coincident(g9,g10)
    c: Coincident(g11,g9)
    c: Radius(g9) = 4.32
    c: Coincident(g7,g-13)
    c: Coincident(g10,g-14)
    c: Coincident(g9,g-3)
    c: Vertical(g9,g-5)
    c: Horizontal(g-4,g9)
    c: Coincident(g-9,g6)
    c: Vertical(g6,g-9)
    c: Horizontal(g-9,g6)
FEATURE [PartDesign::Pad] Pad007  label="EnclosureReinforcements"
  BaseFeature = -> Fillet003
  Direction = (0,1,-2e-16)
  Length = 10
  Length2 = 10
  Profile = -> Sketch014
  ReferenceAxis = -> Sketch014 [N_Axis]
  Refine = true
  Suppressed = false
  Type = 3
  UpToFace = -> Fillet003 [Face2]
FEATURE [Sketcher::SketchObject] Sketch015
  ArcFitTolerance = 1e-06
  AttachmentSupport = -> [Pad007]
  ExternalGeometry = -> [Binder001]
  FullyConstrained = true
  MakeInternals = false
  MapMode = 5
  Placement = pos=(0,-20,5.2e-15) rot=(0,0.707107,0.707107;3.14159rad)
  sketch-geometry (4):
    g0: Circle CenterX=-15 CenterY=22.42 CenterZ=0 NormalX=0 NormalY=0 NormalZ=1 AngleXU=0 Radius=1.2
    g1: Circle CenterX=15.64 CenterY=22.42 CenterZ=0 NormalX=0 NormalY=0 NormalZ=1 AngleXU=0 Radius=1.2
    g2: Circle CenterX=15.64 CenterY=-38.22 CenterZ=0 NormalX=0 NormalY=0 NormalZ=1 AngleXU=0 Radius=1.2
    g3: Circle CenterX=-15 CenterY=-38.22 CenterZ=0 NormalX=0 NormalY=0 NormalZ=1 AngleXU=0 Radius=1.2
  constraints (8):
    c: Coincident(g0,g-3)
    c: Equal(g0,g-3)
    c: Coincident(g1,g-4)
    c: Equal(g1,g-4)
    c: Coincident(g2,g-5)
    c: Equal(g2,g-5)
    c: Coincident(g3,g-6)
    c: Equal(g3,g-6)
FEATURE [PartDesign::Hole] Hole003  label="EnclosureScrewHoles001"
  BaseFeature = -> Pad007
  CustomThreadClearance = 0
  Depth = 16
  DepthType = 0
  Diameter = 1.6
  DrillForDepth = false
  DrillPoint = 1
  DrillPointAngle = 118
  HoleCutCountersinkAngle = 90
  HoleCutCustomValues = false
  HoleCutDepth = 0
  HoleCutDiameter = 6.1
  HoleCutType = 0
  ModelThread = false
  Profile = -> Sketch015
  Refine = true
  Suppressed = false
  Tapered = false
  TaperedAngle = 90
  ThreadClass = 0
  ThreadDepth = 16
  ThreadDepthType = 0
  ThreadDirection = 0
  ThreadFit = 0
  ThreadSize = 6
  ThreadType = 1
  Threaded = true
  UseCustomThreadClearance = false
  expr: Depth = <<Spreadsheet_Enclosure>>.EnclosureTopDepth - <<Spreadsheet_Enclosure>>.EnclosureWallThickness
FEATURE [Sketcher::SketchObject] Sketch016
  ArcFitTolerance = 1e-06
  AttachmentSupport = -> [Hole003]
  ExternalGeometry = -> [Binder002]
  FullyConstrained = true
  MakeInternals = false
  MapMode = 5
  Placement = pos=(0,-40,1.04e-14) rot=(1,0,0;1.5708rad)
  sketch-geometry (4):
    g0: LineSegment StartX=-2 StartY=12.2 StartZ=0 EndX=-2 EndY=9.62 EndZ=0
    g1: LineSegment StartX=-2 StartY=9.62 StartZ=0 EndX=2 EndY=9.62 EndZ=0
    g2: LineSegment StartX=2 StartY=9.62 StartZ=0 EndX=2 EndY=12.2 EndZ=0
    g3: LineSegment StartX=2 StartY=12.2 StartZ=0 EndX=-2 EndY=12.2 EndZ=0
  constraints (10):
    c: Coincident(g0,g1)
    c: Coincident(g1,g2)
    c: Coincident(g2,g3)
    c: Coincident(g3,g0)
    c: Vertical(g0)
    c: Vertical(g2)
    c: Horizontal(g1)
    c: Horizontal(g3)
    c: Coincident(g0,g-6)
    c: Coincident(g1,g-5)
FEATURE [PartDesign::Pocket] Pocket004  label="ResetButtonHole"
  BaseFeature = -> Hole003
  Direction = (0,1,-2e-16)
  Length = 5
  Length2 = 5
  Profile = -> Sketch016
  ReferenceAxis = -> Sketch016 [N_Axis]
  Refine = true
  Suppressed = false
  Type = 1
FEATURE [PartDesign::SubShapeBinder] Binder005  label="Binder_SlideSwitch"
  BindCopyOnChange = 0
  BindMode = 0
  ClaimChildren = false
  Context = -> Assembly001 [Assembly002.Part002.Body002.Binder005.]
  Fuse = false
  MakeFace = true
  OffsetFill = false
  OffsetIntersection = false
  OffsetJoinType = 0
  OffsetOpenResult = false
  PartialLoad = false
  Refine = true
  Relative = true
  Support = -> [SP2T_Switch]
  _Version = 2
FEATURE [Sketcher::SketchObject] Sketch017
  ArcFitTolerance = 1e-06
  AttachmentSupport = -> [Pocket004]
  ExternalGeometry = -> [Binder005]
  FullyConstrained = true
  MakeInternals = false
  MapMode = 5
  Placement = pos=(0,-40,1.04e-14) rot=(1,0,0;1.5708rad)
  sketch-geometry (4):
    g0: LineSegment StartX=-1.89086 StartY=2.35379 StartZ=0 EndX=-1.89086 EndY=-3.64621 EndZ=0
    g1: LineSegment StartX=-1.89086 StartY=-3.64621 StartZ=0 EndX=1.50914 EndY=-3.64621 EndZ=0
    g2: LineSegment StartX=1.50914 StartY=-3.64621 StartZ=0 EndX=1.50914 EndY=2.35379 EndZ=0
    g3: LineSegment StartX=1.50914 StartY=2.35379 StartZ=0 EndX=-1.89086 EndY=2.35379 EndZ=0
  constraints (10):
    c: Coincident(g0,g1)
    c: Coincident(g1,g2)
    c: Coincident(g2,g3)
    c: Coincident(g3,g0)
    c: Vertical(g0)
    c: Vertical(g2)
    c: Horizontal(g1)
    c: Horizontal(g3)
    c: Coincident(g0,g-3)
    c: Coincident(g1,g-5)
FEATURE [PartDesign::Pocket] Pocket005  label="SlideSwitchHole"
  BaseFeature = -> Pocket004
  Direction = (0,1,-2e-16)
  Length = 15
  Length2 = 5
  Profile = -> Sketch017
  ReferenceAxis = -> Sketch017 [N_Axis]
  Refine = true
  Suppressed = false
  Type = 0
FEATURE [PartDesign::Body] Body002  label="Body_EnclosureTop"
  AllowCompound = false
  Group = -> [Binder001,Sketch002,Pad002,Thickness001,Binder002,Binder003,Sketch003,Pad003,Sketch004,Pad004,Sketch005,Hole,Sketch006,Pad005,Sketch007,Hole001,Sketch008,Pocket,Sketch009,Pocket001,Binder004,Sketch010,Pocket002,Fillet001,Sketch011,Pocket003,Fillet003,Sketch014,Pad007,Sketch015,Hole003,Sketch016,Pocket004,Binder005,Sketch017,Pocket005]
  Origin = -> Origin015
  Tip = -> Pocket005
COMPONENT P6 — geometry summary ("Part_SP2TSwitch"; no construction recipe available for this part):
  bounding box: 19.5 x 11.7 x 6.0 mm
  tessellated surface: 3,572 triangles
  volume: 207 mm^3 (15% of its bounding box)
PROVENANCE & LICENSES
A FreeCAD (.FCStd) document from a public repository crawl; recipes are the document's own serialized feature recipes (and, for linked parts, companion documents' recipes).
License: as declared in the source repository (recorded in the dataset sidecar).
